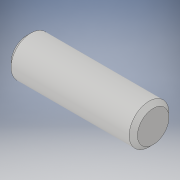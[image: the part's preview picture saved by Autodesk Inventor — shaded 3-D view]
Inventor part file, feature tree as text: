
AUTODESK INVENTOR PART (.ipt)
format: ipt  version: 2018.3 (Build 223284000, 284)  size: 99,840 bytes
history: native  units: in
note: dims shown in document units (in); Inventor stores cm internally (conversion verified against a paired STEP export)
features: revolve x1, chamfer x1, sketch x1
ambient origin geometry x8: Origin, YZ Plane, XZ Plane, XY Plane, X Axis, Y Axis, Z Axis, Center Point
bodies: Solid1 (feature_tree)
feature tree (3):
  revolve  "Revolution1"  [1 undecoded]
  chamfer  "Chamfer1"  Angle=90.0deg  [1 undecoded]
  sketch  "Sketch1"  dims[d0=0.305in d1=0.048in d2=90.0deg d3=0.01in d4=0.125in d5=45.0deg]
note: 2 required parameter values undecoded (feature->parameter linkage not recoverable at this tier; creation-order binding heuristic only, values carry confidence <= 0.55)